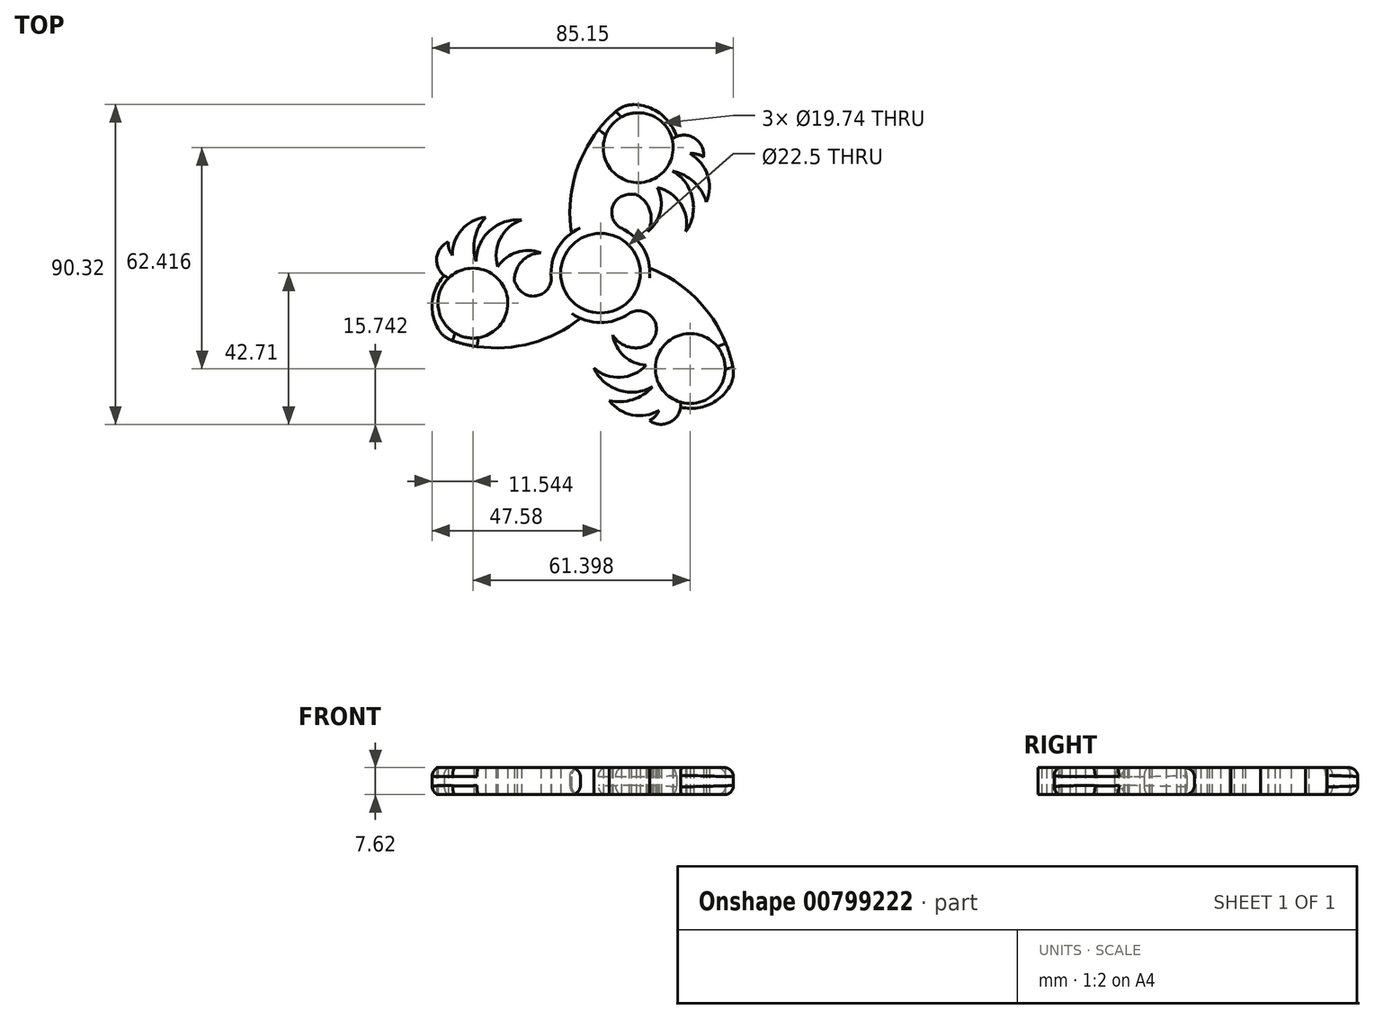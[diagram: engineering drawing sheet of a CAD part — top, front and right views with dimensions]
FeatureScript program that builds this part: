
annotation { "Feature Type Name" : "Feature", "Feature Type Description" : "" }
export const myFeature = defineFeature(function(context is Context, id is Id, definition is map)
    precondition{}
    {
        {
            var Q0;
            Q0=qCreatedBy(makeId("Top.planeOp"),FACE);
            var sketch = newSketch(context, id + "F0", { "sketchPlane" : qUnion([Q0])});
            skCircle(sketch, "E0", {"center": v(0, 0) * mm, "radius": 13.97 * mm});
            skCircle(sketch, "E1", {"center": v(0, 0) * mm, "radius": 11.25 * mm});
            skArc(sketch, "E2", {"start": v(6.16, 47.21) * mm, "mid": v(-5.92, 31.22) * mm, "end": v(-8.2, 11.3) * mm});
            skArc(sketch, "E3", {"start": v(8.66, 22.23) * mm, "mid": v(3.38, 18.59) * mm, "end": v(5.87, 12.68) * mm});
            skArc(sketch, "E4", {"start": v(8.66, 22.23) * mm, "mid": v(21.94, 36.17) * mm, "end": v(6.16, 47.21) * mm});
            skArc(sketch, "E5", {"start": v(13.38, 11.73) * mm, "mid": v(13.96, 17.7) * mm, "end": v(10.05, 22.23) * mm});
            skArc(sketch, "E6", {"start": v(13.38, 11.73) * mm, "mid": v(16.93, 17.48) * mm, "end": v(16.1, 24.18) * mm});
            skArc(sketch, "E7", {"start": v(24.13, 11.73) * mm, "mid": v(22.66, 19.6) * mm, "end": v(16.1, 24.18) * mm});
            skArc(sketch, "E8", {"start": v(24.13, 11.73) * mm, "mid": v(26.03, 21.08) * mm, "end": v(20.44, 28.8) * mm});
            skArc(sketch, "E9", {"start": v(29.93, 20.15) * mm, "mid": v(26.36, 25.77) * mm, "end": v(20.44, 28.8) * mm});
            skArc(sketch, "E10", {"start": v(29.93, 20.15) * mm, "mid": v(29.5, 29.45) * mm, "end": v(22, 34.96) * mm});
            skArc(sketch, "E11", {"start": v(29.15, 32.85) * mm, "mid": v(26.92, 37.87) * mm, "end": v(21.46, 38.58) * mm});
            skArc(sketch, "E12", {"start": v(29.15, 32.85) * mm, "mid": v(25.33, 33.77) * mm, "end": v(21.72, 32.23) * mm});
            skArc(sketch, "E13.1.0", {"start": v(-32.41, 15.84) * mm, "mid": v(-40.25, 10.82) * mm, "end": v(-41.28, 1.57) * mm});
            skArc(sketch, "E13.1.1", {"start": v(-22.22, 15.03) * mm, "mid": v(-31.27, 12) * mm, "end": v(-35.17, 3.3) * mm});
            skArc(sketch, "E13.1.2", {"start": v(-43.97, -18.27) * mm, "mid": v(-24.08, -20.73) * mm, "end": v(-5.69, -12.76) * mm});
            skArc(sketch, "E13.1.3", {"start": v(-32.41, 15.84) * mm, "mid": v(-35.5, 9.95) * mm, "end": v(-35.17, 3.3) * mm});
            skArc(sketch, "E13.1.4", {"start": v(-23.58, -3.61) * mm, "mid": v(-17.79, -6.37) * mm, "end": v(-13.91, -1.26) * mm});
            skArc(sketch, "E13.1.5", {"start": v(-43.03, 8.82) * mm, "mid": v(-46.26, 4.37) * mm, "end": v(-44.14, -0.7) * mm});
            skArc(sketch, "E13.1.6", {"start": v(-22.22, 15.03) * mm, "mid": v(-28.3, 9.82) * mm, "end": v(-28.99, 1.85) * mm});
            skArc(sketch, "E13.1.7", {"start": v(-23.58, -3.61) * mm, "mid": v(-42.3, 0.91) * mm, "end": v(-43.97, -18.27) * mm});
            skArc(sketch, "E13.1.8", {"start": v(-43.03, 8.82) * mm, "mid": v(-41.9, 5.06) * mm, "end": v(-38.77, 2.7) * mm});
            skArc(sketch, "E13.1.9", {"start": v(-16.85, 5.72) * mm, "mid": v(-23.6, 5.93) * mm, "end": v(-28.99, 1.85) * mm});
            skArc(sketch, "E13.1.10", {"start": v(-16.85, 5.72) * mm, "mid": v(-22.3, 3.24) * mm, "end": v(-24.28, -2.41) * mm});
            skArc(sketch, "E13.2.0", {"start": v(2.49, -36) * mm, "mid": v(10.75, -40.27) * mm, "end": v(19.28, -36.54) * mm});
            skArc(sketch, "E13.2.1", {"start": v(-1.9, -26.76) * mm, "mid": v(5.24, -33.08) * mm, "end": v(14.73, -32.1) * mm});
            skArc(sketch, "E13.2.2", {"start": v(37.8, -28.94) * mm, "mid": v(30, -10.48) * mm, "end": v(13.9, 1.45) * mm});
            skArc(sketch, "E13.2.3", {"start": v(2.49, -36) * mm, "mid": v(9.13, -35.71) * mm, "end": v(14.73, -32.1) * mm});
            skArc(sketch, "E13.2.4", {"start": v(14.92, -18.61) * mm, "mid": v(14.4, -12.22) * mm, "end": v(8.05, -11.42) * mm});
            skArc(sketch, "E13.2.5", {"start": v(13.87, -41.67) * mm, "mid": v(19.34, -42.25) * mm, "end": v(22.68, -37.87) * mm});
            skArc(sketch, "E13.2.6", {"start": v(-1.9, -26.76) * mm, "mid": v(5.64, -29.43) * mm, "end": v(12.9, -26.03) * mm});
            skArc(sketch, "E13.2.7", {"start": v(14.92, -18.61) * mm, "mid": v(20.36, -37.09) * mm, "end": v(37.8, -28.94) * mm});
            skArc(sketch, "E13.2.8", {"start": v(13.87, -41.67) * mm, "mid": v(16.58, -38.82) * mm, "end": v(17.06, -34.92) * mm});
            skArc(sketch, "E13.2.9", {"start": v(3.47, -17.46) * mm, "mid": v(6.67, -23.4) * mm, "end": v(12.9, -26.03) * mm});
            skArc(sketch, "E13.2.10", {"start": v(3.47, -17.46) * mm, "mid": v(8.34, -20.94) * mm, "end": v(14.23, -19.82) * mm});
            skCircle(sketch, "E14", {"center": v(10.67, 35.45) * mm, "radius": 9.87 * mm});
            skCircle(sketch, "E15.1.0", {"center": v(-36.04, -8.48) * mm, "radius": 9.87 * mm});
            skCircle(sketch, "E15.2.0", {"center": v(25.36, -26.97) * mm, "radius": 9.87 * mm});
            skSolve(sketch);
        }
        {
            var Q0;
            {var subQ3=sQuery(id+"F0.wireOp",EDGE,"E13.1.2");Q0=makeQuery(id+"F0.imprint","IMPRINT",FACE,{"disambiguationData":[TD([[makeQuery(id+"F0.imprint","IMPRINT",EDGE,{"derivedFrom":subQ3}),1.0]])]});}
            var Q1;
            Q1=makeQuery(id+"F0.imprint","IMPRINT",FACE,{"disambiguationData":[TD([[makeQuery(id+"F0.imprint","IMPRINT",EDGE,{"derivedFrom":sQuery(id+"F0.wireOp",EDGE,"E1")}),-1.0]])]});
            var Q2;
            {var subQ5=sQuery(id+"F0.wireOp",EDGE,"E13.1.5");Q2=makeQuery(id+"F0.imprint","IMPRINT",FACE,{"disambiguationData":[TD([[makeQuery(id+"F0.imprint","IMPRINT",EDGE,{"derivedFrom":subQ5}),1.0]])]});}
            var Q3;
            {var subQ0=sQuery(id+"F0.wireOp",EDGE,"E13.1.3");Q3=makeQuery(id+"F0.imprint","IMPRINT",FACE,{"disambiguationData":[TD([[makeQuery(id+"F0.imprint","IMPRINT",EDGE,{"derivedFrom":subQ0}),-1.0]])]});}
            var Q4;
            {var subQ0=sQuery(id+"F0.wireOp",EDGE,"E13.1.7");var subQ1=sQuery(id+"F0.wireOp",EDGE,"E13.1.0");var subQ2=makeQuery(id+"F0.imprint","INTERSECT",VERTEX,{"derivedFrom":[subQ1,subQ0]});Q4=makeQuery(id+"F0.imprint","IMPRINT",FACE,{"disambiguationData":[TD([[makeQuery(id+"F0.imprint","IMPRINT",EDGE,{"disambiguationData":[TD([[subQ2,1.0]])],"derivedFrom":subQ1}),1.0]])]});}
            var Q5;
            {var subQ0=sQuery(id+"F0.wireOp",EDGE,"E13.1.1");Q5=makeQuery(id+"F0.imprint","IMPRINT",FACE,{"disambiguationData":[TD([[makeQuery(id+"F0.imprint","IMPRINT",EDGE,{"derivedFrom":subQ0}),1.0]])]});}
            var Q6;
            {var subQ0=sQuery(id+"F0.wireOp",EDGE,"E13.1.9");Q6=makeQuery(id+"F0.imprint","IMPRINT",FACE,{"disambiguationData":[TD([[makeQuery(id+"F0.imprint","IMPRINT",EDGE,{"derivedFrom":subQ0}),1.0]])]});}
            var Q7;
            {var subQ3=sQuery(id+"F0.wireOp",EDGE,"E2");Q7=makeQuery(id+"F0.imprint","IMPRINT",FACE,{"disambiguationData":[TD([[makeQuery(id+"F0.imprint","IMPRINT",EDGE,{"derivedFrom":subQ3}),1.0]])]});}
            var Q8;
            {var subQ3=sQuery(id+"F0.wireOp",EDGE,"E13.2.2");Q8=makeQuery(id+"F0.imprint","IMPRINT",FACE,{"disambiguationData":[TD([[makeQuery(id+"F0.imprint","IMPRINT",EDGE,{"derivedFrom":subQ3}),1.0]])]});}
            var Q9;
            {var subQ3=sQuery(id+"F0.wireOp",EDGE,"E11");Q9=makeQuery(id+"F0.imprint","IMPRINT",FACE,{"disambiguationData":[TD([[makeQuery(id+"F0.imprint","IMPRINT",EDGE,{"derivedFrom":subQ3}),1.0]])]});}
            var Q10;
            {var subQ0=sQuery(id+"F0.wireOp",EDGE,"E9");Q10=makeQuery(id+"F0.imprint","IMPRINT",FACE,{"disambiguationData":[TD([[makeQuery(id+"F0.imprint","IMPRINT",EDGE,{"derivedFrom":subQ0}),-1.0]])]});}
            var Q11;
            {var subQ0=sQuery(id+"F0.wireOp",EDGE,"E7");Q11=makeQuery(id+"F0.imprint","IMPRINT",FACE,{"disambiguationData":[TD([[makeQuery(id+"F0.imprint","IMPRINT",EDGE,{"derivedFrom":subQ0}),-1.0]])]});}
            var Q12;
            {var subQ0=sQuery(id+"F0.wireOp",EDGE,"E5");Q12=makeQuery(id+"F0.imprint","IMPRINT",FACE,{"disambiguationData":[TD([[makeQuery(id+"F0.imprint","IMPRINT",EDGE,{"derivedFrom":subQ0}),-1.0]])]});}
            var Q13;
            {var subQ0=sQuery(id+"F0.wireOp",EDGE,"E10");var subQ1=sQuery(id+"F0.wireOp",EDGE,"E4");var subQ2=makeQuery(id+"F0.imprint","INTERSECT",VERTEX,{"derivedFrom":[subQ1,subQ0]});Q13=makeQuery(id+"F0.imprint","IMPRINT",FACE,{"disambiguationData":[TD([[makeQuery(id+"F0.imprint","IMPRINT",EDGE,{"disambiguationData":[TD([[subQ2,1.0]])],"derivedFrom":subQ1}),-1.0]])]});}
            var Q14;
            {var subQ0=sQuery(id+"F0.wireOp",EDGE,"E13.2.9");Q14=makeQuery(id+"F0.imprint","IMPRINT",FACE,{"disambiguationData":[TD([[makeQuery(id+"F0.imprint","IMPRINT",EDGE,{"derivedFrom":subQ0}),1.0]])]});}
            var Q15;
            {var subQ0=sQuery(id+"F0.wireOp",EDGE,"E13.2.1");Q15=makeQuery(id+"F0.imprint","IMPRINT",FACE,{"disambiguationData":[TD([[makeQuery(id+"F0.imprint","IMPRINT",EDGE,{"derivedFrom":subQ0}),1.0]])]});}
            var Q16;
            {var subQ5=sQuery(id+"F0.wireOp",EDGE,"E13.2.5");Q16=makeQuery(id+"F0.imprint","IMPRINT",FACE,{"disambiguationData":[TD([[makeQuery(id+"F0.imprint","IMPRINT",EDGE,{"derivedFrom":subQ5}),1.0]])]});}
            var Q17;
            {var subQ0=sQuery(id+"F0.wireOp",EDGE,"E13.2.3");Q17=makeQuery(id+"F0.imprint","IMPRINT",FACE,{"disambiguationData":[TD([[makeQuery(id+"F0.imprint","IMPRINT",EDGE,{"derivedFrom":subQ0}),-1.0]])]});}
            var Q18;
            {var subQ0=sQuery(id+"F0.wireOp",EDGE,"E13.2.7");var subQ1=sQuery(id+"F0.wireOp",EDGE,"E13.2.0");var subQ2=makeQuery(id+"F0.imprint","INTERSECT",VERTEX,{"derivedFrom":[subQ1,subQ0]});Q18=makeQuery(id+"F0.imprint","IMPRINT",FACE,{"disambiguationData":[TD([[makeQuery(id+"F0.imprint","IMPRINT",EDGE,{"disambiguationData":[TD([[subQ2,1.0]])],"derivedFrom":subQ1}),1.0]])]});}
            extrude(context, id + "F1", {"entities" : qUnion([Q0, Q1, Q2, Q3, Q4, Q5, Q6, Q7, Q8, Q9, Q10, Q11, Q12, Q13, Q14, Q15, Q16, Q17, Q18]), "depth" : 7.62 * mm, "offsetDistance" : 25.4 * mm});
        }
        {
            var Q0;
            Q0=makeQuery(id+"F1.opExtrude","SWEPT_EDGE",EDGE,{"disambiguationData":[OSD([sQuery(id+"F0.wireOp",EDGE,"E13.2.2"),sQuery(id+"F0.wireOp",EDGE,"E13.2.7")])]});
            var Q1;
            Q1=makeQuery(id+"F1.opExtrude","SWEPT_EDGE",EDGE,{"disambiguationData":[OSD([sQuery(id+"F0.wireOp",EDGE,"E2"),sQuery(id+"F0.wireOp",EDGE,"E4")])]});
            var Q2;
            Q2=makeQuery(id+"F1.opExtrude","SWEPT_EDGE",EDGE,{"disambiguationData":[OSD([sQuery(id+"F0.wireOp",EDGE,"E13.1.2"),sQuery(id+"F0.wireOp",EDGE,"E13.1.7")])]});
            fillet(context, id + "F2", {"entities" : qUnion([Q0, Q1, Q2]), "radius" : 7.62 * mm, "tangentPropagation" : true, "allowEdgeOverflow" : false});
        }
        {
            var Q0;
            {var subQ0=sQuery(id+"F0.wireOp",EDGE,"E13.1.7");var subQ1=sQuery(id+"F0.wireOp",EDGE,"E13.1.2");Q0=makeQuery(id+"F2.opFillet","BLEND_EDGE",EDGE,{"blendedFrom":[makeQuery(id+"F1.opExtrude","SWEPT_EDGE",EDGE,{"disambiguationData":[OSD([subQ1,subQ0])]}),makeQuery(id+"F1.opExtrude","CAP_FACE",FACE,{"disambiguationData":[OSD([sQuery(id+"F0.wireOp",EDGE,"E0"),sQuery(id+"F0.wireOp",EDGE,"E1"),sQuery(id+"F0.wireOp",EDGE,"E2"),sQuery(id+"F0.wireOp",EDGE,"E3"),sQuery(id+"F0.wireOp",EDGE,"E4"),sQuery(id+"F0.wireOp",EDGE,"E5"),sQuery(id+"F0.wireOp",EDGE,"E6"),sQuery(id+"F0.wireOp",EDGE,"E7"),sQuery(id+"F0.wireOp",EDGE,"E8"),sQuery(id+"F0.wireOp",EDGE,"E9"),sQuery(id+"F0.wireOp",EDGE,"E10"),sQuery(id+"F0.wireOp",EDGE,"E11"),sQuery(id+"F0.wireOp",EDGE,"E12"),sQuery(id+"F0.wireOp",EDGE,"E13.1.0"),sQuery(id+"F0.wireOp",EDGE,"E13.1.1"),subQ1,sQuery(id+"F0.wireOp",EDGE,"E13.1.3"),sQuery(id+"F0.wireOp",EDGE,"E13.1.4"),sQuery(id+"F0.wireOp",EDGE,"E13.1.5"),sQuery(id+"F0.wireOp",EDGE,"E13.1.6"),subQ0,sQuery(id+"F0.wireOp",EDGE,"E13.1.8"),sQuery(id+"F0.wireOp",EDGE,"E13.1.9"),sQuery(id+"F0.wireOp",EDGE,"E13.1.10"),sQuery(id+"F0.wireOp",EDGE,"E13.2.0"),sQuery(id+"F0.wireOp",EDGE,"E13.2.1"),sQuery(id+"F0.wireOp",EDGE,"E13.2.2"),sQuery(id+"F0.wireOp",EDGE,"E13.2.3"),sQuery(id+"F0.wireOp",EDGE,"E13.2.4"),sQuery(id+"F0.wireOp",EDGE,"E13.2.5"),sQuery(id+"F0.wireOp",EDGE,"E13.2.6"),sQuery(id+"F0.wireOp",EDGE,"E13.2.7"),sQuery(id+"F0.wireOp",EDGE,"E13.2.8"),sQuery(id+"F0.wireOp",EDGE,"E13.2.9"),sQuery(id+"F0.wireOp",EDGE,"E13.2.10"),sQuery(id+"F0.wireOp",EDGE,"E14"),sQuery(id+"F0.wireOp",EDGE,"E15.1.0"),sQuery(id+"F0.wireOp",EDGE,"E15.2.0")])],"isStart":false})],"blendedInto":[makeQuery(id+"F1.opExtrude","CAP_FACE",FACE,{"disambiguationData":[OSD([sQuery(id+"F0.wireOp",EDGE,"E0"),sQuery(id+"F0.wireOp",EDGE,"E1"),sQuery(id+"F0.wireOp",EDGE,"E2"),sQuery(id+"F0.wireOp",EDGE,"E3"),sQuery(id+"F0.wireOp",EDGE,"E4"),sQuery(id+"F0.wireOp",EDGE,"E5"),sQuery(id+"F0.wireOp",EDGE,"E6"),sQuery(id+"F0.wireOp",EDGE,"E7"),sQuery(id+"F0.wireOp",EDGE,"E8"),sQuery(id+"F0.wireOp",EDGE,"E9"),sQuery(id+"F0.wireOp",EDGE,"E10"),sQuery(id+"F0.wireOp",EDGE,"E11"),sQuery(id+"F0.wireOp",EDGE,"E12"),sQuery(id+"F0.wireOp",EDGE,"E13.1.0"),sQuery(id+"F0.wireOp",EDGE,"E13.1.1"),subQ1,sQuery(id+"F0.wireOp",EDGE,"E13.1.3"),sQuery(id+"F0.wireOp",EDGE,"E13.1.4"),sQuery(id+"F0.wireOp",EDGE,"E13.1.5"),sQuery(id+"F0.wireOp",EDGE,"E13.1.6"),subQ0,sQuery(id+"F0.wireOp",EDGE,"E13.1.8"),sQuery(id+"F0.wireOp",EDGE,"E13.1.9"),sQuery(id+"F0.wireOp",EDGE,"E13.1.10"),sQuery(id+"F0.wireOp",EDGE,"E13.2.0"),sQuery(id+"F0.wireOp",EDGE,"E13.2.1"),sQuery(id+"F0.wireOp",EDGE,"E13.2.2"),sQuery(id+"F0.wireOp",EDGE,"E13.2.3"),sQuery(id+"F0.wireOp",EDGE,"E13.2.4"),sQuery(id+"F0.wireOp",EDGE,"E13.2.5"),sQuery(id+"F0.wireOp",EDGE,"E13.2.6"),sQuery(id+"F0.wireOp",EDGE,"E13.2.7"),sQuery(id+"F0.wireOp",EDGE,"E13.2.8"),sQuery(id+"F0.wireOp",EDGE,"E13.2.9"),sQuery(id+"F0.wireOp",EDGE,"E13.2.10"),sQuery(id+"F0.wireOp",EDGE,"E14"),sQuery(id+"F0.wireOp",EDGE,"E15.1.0"),sQuery(id+"F0.wireOp",EDGE,"E15.2.0")])],"isStart":false})]});}
            var Q1;
            {var subQ0=sQuery(id+"F0.wireOp",EDGE,"E13.2.7");var subQ1=sQuery(id+"F0.wireOp",EDGE,"E13.2.2");Q1=makeQuery(id+"F2.opFillet","BLEND_EDGE",EDGE,{"blendedFrom":[makeQuery(id+"F1.opExtrude","SWEPT_EDGE",EDGE,{"disambiguationData":[OSD([subQ1,subQ0])]}),makeQuery(id+"F1.opExtrude","CAP_FACE",FACE,{"disambiguationData":[OSD([sQuery(id+"F0.wireOp",EDGE,"E0"),sQuery(id+"F0.wireOp",EDGE,"E1"),sQuery(id+"F0.wireOp",EDGE,"E2"),sQuery(id+"F0.wireOp",EDGE,"E3"),sQuery(id+"F0.wireOp",EDGE,"E4"),sQuery(id+"F0.wireOp",EDGE,"E5"),sQuery(id+"F0.wireOp",EDGE,"E6"),sQuery(id+"F0.wireOp",EDGE,"E7"),sQuery(id+"F0.wireOp",EDGE,"E8"),sQuery(id+"F0.wireOp",EDGE,"E9"),sQuery(id+"F0.wireOp",EDGE,"E10"),sQuery(id+"F0.wireOp",EDGE,"E11"),sQuery(id+"F0.wireOp",EDGE,"E12"),sQuery(id+"F0.wireOp",EDGE,"E13.1.0"),sQuery(id+"F0.wireOp",EDGE,"E13.1.1"),sQuery(id+"F0.wireOp",EDGE,"E13.1.2"),sQuery(id+"F0.wireOp",EDGE,"E13.1.3"),sQuery(id+"F0.wireOp",EDGE,"E13.1.4"),sQuery(id+"F0.wireOp",EDGE,"E13.1.5"),sQuery(id+"F0.wireOp",EDGE,"E13.1.6"),sQuery(id+"F0.wireOp",EDGE,"E13.1.7"),sQuery(id+"F0.wireOp",EDGE,"E13.1.8"),sQuery(id+"F0.wireOp",EDGE,"E13.1.9"),sQuery(id+"F0.wireOp",EDGE,"E13.1.10"),sQuery(id+"F0.wireOp",EDGE,"E13.2.0"),sQuery(id+"F0.wireOp",EDGE,"E13.2.1"),subQ1,sQuery(id+"F0.wireOp",EDGE,"E13.2.3"),sQuery(id+"F0.wireOp",EDGE,"E13.2.4"),sQuery(id+"F0.wireOp",EDGE,"E13.2.5"),sQuery(id+"F0.wireOp",EDGE,"E13.2.6"),subQ0,sQuery(id+"F0.wireOp",EDGE,"E13.2.8"),sQuery(id+"F0.wireOp",EDGE,"E13.2.9"),sQuery(id+"F0.wireOp",EDGE,"E13.2.10"),sQuery(id+"F0.wireOp",EDGE,"E14"),sQuery(id+"F0.wireOp",EDGE,"E15.1.0"),sQuery(id+"F0.wireOp",EDGE,"E15.2.0")])],"isStart":false})],"blendedInto":[makeQuery(id+"F1.opExtrude","CAP_FACE",FACE,{"disambiguationData":[OSD([sQuery(id+"F0.wireOp",EDGE,"E0"),sQuery(id+"F0.wireOp",EDGE,"E1"),sQuery(id+"F0.wireOp",EDGE,"E2"),sQuery(id+"F0.wireOp",EDGE,"E3"),sQuery(id+"F0.wireOp",EDGE,"E4"),sQuery(id+"F0.wireOp",EDGE,"E5"),sQuery(id+"F0.wireOp",EDGE,"E6"),sQuery(id+"F0.wireOp",EDGE,"E7"),sQuery(id+"F0.wireOp",EDGE,"E8"),sQuery(id+"F0.wireOp",EDGE,"E9"),sQuery(id+"F0.wireOp",EDGE,"E10"),sQuery(id+"F0.wireOp",EDGE,"E11"),sQuery(id+"F0.wireOp",EDGE,"E12"),sQuery(id+"F0.wireOp",EDGE,"E13.1.0"),sQuery(id+"F0.wireOp",EDGE,"E13.1.1"),sQuery(id+"F0.wireOp",EDGE,"E13.1.2"),sQuery(id+"F0.wireOp",EDGE,"E13.1.3"),sQuery(id+"F0.wireOp",EDGE,"E13.1.4"),sQuery(id+"F0.wireOp",EDGE,"E13.1.5"),sQuery(id+"F0.wireOp",EDGE,"E13.1.6"),sQuery(id+"F0.wireOp",EDGE,"E13.1.7"),sQuery(id+"F0.wireOp",EDGE,"E13.1.8"),sQuery(id+"F0.wireOp",EDGE,"E13.1.9"),sQuery(id+"F0.wireOp",EDGE,"E13.1.10"),sQuery(id+"F0.wireOp",EDGE,"E13.2.0"),sQuery(id+"F0.wireOp",EDGE,"E13.2.1"),subQ1,sQuery(id+"F0.wireOp",EDGE,"E13.2.3"),sQuery(id+"F0.wireOp",EDGE,"E13.2.4"),sQuery(id+"F0.wireOp",EDGE,"E13.2.5"),sQuery(id+"F0.wireOp",EDGE,"E13.2.6"),subQ0,sQuery(id+"F0.wireOp",EDGE,"E13.2.8"),sQuery(id+"F0.wireOp",EDGE,"E13.2.9"),sQuery(id+"F0.wireOp",EDGE,"E13.2.10"),sQuery(id+"F0.wireOp",EDGE,"E14"),sQuery(id+"F0.wireOp",EDGE,"E15.1.0"),sQuery(id+"F0.wireOp",EDGE,"E15.2.0")])],"isStart":false})]});}
            var Q2;
            {var subQ0=sQuery(id+"F0.wireOp",EDGE,"E4");var subQ1=sQuery(id+"F0.wireOp",EDGE,"E2");Q2=makeQuery(id+"F2.opFillet","BLEND_EDGE",EDGE,{"blendedFrom":[makeQuery(id+"F1.opExtrude","SWEPT_EDGE",EDGE,{"disambiguationData":[OSD([subQ1,subQ0])]}),makeQuery(id+"F1.opExtrude","CAP_FACE",FACE,{"disambiguationData":[OSD([sQuery(id+"F0.wireOp",EDGE,"E0"),sQuery(id+"F0.wireOp",EDGE,"E1"),subQ1,sQuery(id+"F0.wireOp",EDGE,"E3"),subQ0,sQuery(id+"F0.wireOp",EDGE,"E5"),sQuery(id+"F0.wireOp",EDGE,"E6"),sQuery(id+"F0.wireOp",EDGE,"E7"),sQuery(id+"F0.wireOp",EDGE,"E8"),sQuery(id+"F0.wireOp",EDGE,"E9"),sQuery(id+"F0.wireOp",EDGE,"E10"),sQuery(id+"F0.wireOp",EDGE,"E11"),sQuery(id+"F0.wireOp",EDGE,"E12"),sQuery(id+"F0.wireOp",EDGE,"E13.1.0"),sQuery(id+"F0.wireOp",EDGE,"E13.1.1"),sQuery(id+"F0.wireOp",EDGE,"E13.1.2"),sQuery(id+"F0.wireOp",EDGE,"E13.1.3"),sQuery(id+"F0.wireOp",EDGE,"E13.1.4"),sQuery(id+"F0.wireOp",EDGE,"E13.1.5"),sQuery(id+"F0.wireOp",EDGE,"E13.1.6"),sQuery(id+"F0.wireOp",EDGE,"E13.1.7"),sQuery(id+"F0.wireOp",EDGE,"E13.1.8"),sQuery(id+"F0.wireOp",EDGE,"E13.1.9"),sQuery(id+"F0.wireOp",EDGE,"E13.1.10"),sQuery(id+"F0.wireOp",EDGE,"E13.2.0"),sQuery(id+"F0.wireOp",EDGE,"E13.2.1"),sQuery(id+"F0.wireOp",EDGE,"E13.2.2"),sQuery(id+"F0.wireOp",EDGE,"E13.2.3"),sQuery(id+"F0.wireOp",EDGE,"E13.2.4"),sQuery(id+"F0.wireOp",EDGE,"E13.2.5"),sQuery(id+"F0.wireOp",EDGE,"E13.2.6"),sQuery(id+"F0.wireOp",EDGE,"E13.2.7"),sQuery(id+"F0.wireOp",EDGE,"E13.2.8"),sQuery(id+"F0.wireOp",EDGE,"E13.2.9"),sQuery(id+"F0.wireOp",EDGE,"E13.2.10"),sQuery(id+"F0.wireOp",EDGE,"E14"),sQuery(id+"F0.wireOp",EDGE,"E15.1.0"),sQuery(id+"F0.wireOp",EDGE,"E15.2.0")])],"isStart":false})],"blendedInto":[makeQuery(id+"F1.opExtrude","CAP_FACE",FACE,{"disambiguationData":[OSD([sQuery(id+"F0.wireOp",EDGE,"E0"),sQuery(id+"F0.wireOp",EDGE,"E1"),subQ1,sQuery(id+"F0.wireOp",EDGE,"E3"),subQ0,sQuery(id+"F0.wireOp",EDGE,"E5"),sQuery(id+"F0.wireOp",EDGE,"E6"),sQuery(id+"F0.wireOp",EDGE,"E7"),sQuery(id+"F0.wireOp",EDGE,"E8"),sQuery(id+"F0.wireOp",EDGE,"E9"),sQuery(id+"F0.wireOp",EDGE,"E10"),sQuery(id+"F0.wireOp",EDGE,"E11"),sQuery(id+"F0.wireOp",EDGE,"E12"),sQuery(id+"F0.wireOp",EDGE,"E13.1.0"),sQuery(id+"F0.wireOp",EDGE,"E13.1.1"),sQuery(id+"F0.wireOp",EDGE,"E13.1.2"),sQuery(id+"F0.wireOp",EDGE,"E13.1.3"),sQuery(id+"F0.wireOp",EDGE,"E13.1.4"),sQuery(id+"F0.wireOp",EDGE,"E13.1.5"),sQuery(id+"F0.wireOp",EDGE,"E13.1.6"),sQuery(id+"F0.wireOp",EDGE,"E13.1.7"),sQuery(id+"F0.wireOp",EDGE,"E13.1.8"),sQuery(id+"F0.wireOp",EDGE,"E13.1.9"),sQuery(id+"F0.wireOp",EDGE,"E13.1.10"),sQuery(id+"F0.wireOp",EDGE,"E13.2.0"),sQuery(id+"F0.wireOp",EDGE,"E13.2.1"),sQuery(id+"F0.wireOp",EDGE,"E13.2.2"),sQuery(id+"F0.wireOp",EDGE,"E13.2.3"),sQuery(id+"F0.wireOp",EDGE,"E13.2.4"),sQuery(id+"F0.wireOp",EDGE,"E13.2.5"),sQuery(id+"F0.wireOp",EDGE,"E13.2.6"),sQuery(id+"F0.wireOp",EDGE,"E13.2.7"),sQuery(id+"F0.wireOp",EDGE,"E13.2.8"),sQuery(id+"F0.wireOp",EDGE,"E13.2.9"),sQuery(id+"F0.wireOp",EDGE,"E13.2.10"),sQuery(id+"F0.wireOp",EDGE,"E14"),sQuery(id+"F0.wireOp",EDGE,"E15.1.0"),sQuery(id+"F0.wireOp",EDGE,"E15.2.0")])],"isStart":false})]});}
            fillet(context, id + "F3", {"entities" : qUnion([Q0, Q1, Q2]), "radius" : 2.54 * mm, "tangentPropagation" : true, "allowEdgeOverflow" : false});
        }
        {
            var Q0;
            {var subQ0=sQuery(id+"F0.wireOp",EDGE,"E4");var subQ1=sQuery(id+"F0.wireOp",EDGE,"E2");Q0=makeQuery(id+"F2.opFillet","BLEND_EDGE",EDGE,{"blendedFrom":[makeQuery(id+"F1.opExtrude","SWEPT_EDGE",EDGE,{"disambiguationData":[OSD([subQ1,subQ0])]}),makeQuery(id+"F1.opExtrude","CAP_FACE",FACE,{"disambiguationData":[OSD([sQuery(id+"F0.wireOp",EDGE,"E0"),sQuery(id+"F0.wireOp",EDGE,"E1"),subQ1,sQuery(id+"F0.wireOp",EDGE,"E3"),subQ0,sQuery(id+"F0.wireOp",EDGE,"E5"),sQuery(id+"F0.wireOp",EDGE,"E6"),sQuery(id+"F0.wireOp",EDGE,"E7"),sQuery(id+"F0.wireOp",EDGE,"E8"),sQuery(id+"F0.wireOp",EDGE,"E9"),sQuery(id+"F0.wireOp",EDGE,"E10"),sQuery(id+"F0.wireOp",EDGE,"E11"),sQuery(id+"F0.wireOp",EDGE,"E12"),sQuery(id+"F0.wireOp",EDGE,"E13.1.0"),sQuery(id+"F0.wireOp",EDGE,"E13.1.1"),sQuery(id+"F0.wireOp",EDGE,"E13.1.2"),sQuery(id+"F0.wireOp",EDGE,"E13.1.3"),sQuery(id+"F0.wireOp",EDGE,"E13.1.4"),sQuery(id+"F0.wireOp",EDGE,"E13.1.5"),sQuery(id+"F0.wireOp",EDGE,"E13.1.6"),sQuery(id+"F0.wireOp",EDGE,"E13.1.7"),sQuery(id+"F0.wireOp",EDGE,"E13.1.8"),sQuery(id+"F0.wireOp",EDGE,"E13.1.9"),sQuery(id+"F0.wireOp",EDGE,"E13.1.10"),sQuery(id+"F0.wireOp",EDGE,"E13.2.0"),sQuery(id+"F0.wireOp",EDGE,"E13.2.1"),sQuery(id+"F0.wireOp",EDGE,"E13.2.2"),sQuery(id+"F0.wireOp",EDGE,"E13.2.3"),sQuery(id+"F0.wireOp",EDGE,"E13.2.4"),sQuery(id+"F0.wireOp",EDGE,"E13.2.5"),sQuery(id+"F0.wireOp",EDGE,"E13.2.6"),sQuery(id+"F0.wireOp",EDGE,"E13.2.7"),sQuery(id+"F0.wireOp",EDGE,"E13.2.8"),sQuery(id+"F0.wireOp",EDGE,"E13.2.9"),sQuery(id+"F0.wireOp",EDGE,"E13.2.10"),sQuery(id+"F0.wireOp",EDGE,"E14"),sQuery(id+"F0.wireOp",EDGE,"E15.1.0"),sQuery(id+"F0.wireOp",EDGE,"E15.2.0")])],"isStart":true})],"blendedInto":[makeQuery(id+"F1.opExtrude","CAP_FACE",FACE,{"disambiguationData":[OSD([sQuery(id+"F0.wireOp",EDGE,"E0"),sQuery(id+"F0.wireOp",EDGE,"E1"),subQ1,sQuery(id+"F0.wireOp",EDGE,"E3"),subQ0,sQuery(id+"F0.wireOp",EDGE,"E5"),sQuery(id+"F0.wireOp",EDGE,"E6"),sQuery(id+"F0.wireOp",EDGE,"E7"),sQuery(id+"F0.wireOp",EDGE,"E8"),sQuery(id+"F0.wireOp",EDGE,"E9"),sQuery(id+"F0.wireOp",EDGE,"E10"),sQuery(id+"F0.wireOp",EDGE,"E11"),sQuery(id+"F0.wireOp",EDGE,"E12"),sQuery(id+"F0.wireOp",EDGE,"E13.1.0"),sQuery(id+"F0.wireOp",EDGE,"E13.1.1"),sQuery(id+"F0.wireOp",EDGE,"E13.1.2"),sQuery(id+"F0.wireOp",EDGE,"E13.1.3"),sQuery(id+"F0.wireOp",EDGE,"E13.1.4"),sQuery(id+"F0.wireOp",EDGE,"E13.1.5"),sQuery(id+"F0.wireOp",EDGE,"E13.1.6"),sQuery(id+"F0.wireOp",EDGE,"E13.1.7"),sQuery(id+"F0.wireOp",EDGE,"E13.1.8"),sQuery(id+"F0.wireOp",EDGE,"E13.1.9"),sQuery(id+"F0.wireOp",EDGE,"E13.1.10"),sQuery(id+"F0.wireOp",EDGE,"E13.2.0"),sQuery(id+"F0.wireOp",EDGE,"E13.2.1"),sQuery(id+"F0.wireOp",EDGE,"E13.2.2"),sQuery(id+"F0.wireOp",EDGE,"E13.2.3"),sQuery(id+"F0.wireOp",EDGE,"E13.2.4"),sQuery(id+"F0.wireOp",EDGE,"E13.2.5"),sQuery(id+"F0.wireOp",EDGE,"E13.2.6"),sQuery(id+"F0.wireOp",EDGE,"E13.2.7"),sQuery(id+"F0.wireOp",EDGE,"E13.2.8"),sQuery(id+"F0.wireOp",EDGE,"E13.2.9"),sQuery(id+"F0.wireOp",EDGE,"E13.2.10"),sQuery(id+"F0.wireOp",EDGE,"E14"),sQuery(id+"F0.wireOp",EDGE,"E15.1.0"),sQuery(id+"F0.wireOp",EDGE,"E15.2.0")])],"isStart":true})]});}
            var Q1;
            {var subQ0=sQuery(id+"F0.wireOp",EDGE,"E13.2.7");var subQ1=sQuery(id+"F0.wireOp",EDGE,"E13.2.2");Q1=makeQuery(id+"F2.opFillet","BLEND_EDGE",EDGE,{"blendedFrom":[makeQuery(id+"F1.opExtrude","SWEPT_EDGE",EDGE,{"disambiguationData":[OSD([subQ1,subQ0])]}),makeQuery(id+"F1.opExtrude","CAP_FACE",FACE,{"disambiguationData":[OSD([sQuery(id+"F0.wireOp",EDGE,"E0"),sQuery(id+"F0.wireOp",EDGE,"E1"),sQuery(id+"F0.wireOp",EDGE,"E2"),sQuery(id+"F0.wireOp",EDGE,"E3"),sQuery(id+"F0.wireOp",EDGE,"E4"),sQuery(id+"F0.wireOp",EDGE,"E5"),sQuery(id+"F0.wireOp",EDGE,"E6"),sQuery(id+"F0.wireOp",EDGE,"E7"),sQuery(id+"F0.wireOp",EDGE,"E8"),sQuery(id+"F0.wireOp",EDGE,"E9"),sQuery(id+"F0.wireOp",EDGE,"E10"),sQuery(id+"F0.wireOp",EDGE,"E11"),sQuery(id+"F0.wireOp",EDGE,"E12"),sQuery(id+"F0.wireOp",EDGE,"E13.1.0"),sQuery(id+"F0.wireOp",EDGE,"E13.1.1"),sQuery(id+"F0.wireOp",EDGE,"E13.1.2"),sQuery(id+"F0.wireOp",EDGE,"E13.1.3"),sQuery(id+"F0.wireOp",EDGE,"E13.1.4"),sQuery(id+"F0.wireOp",EDGE,"E13.1.5"),sQuery(id+"F0.wireOp",EDGE,"E13.1.6"),sQuery(id+"F0.wireOp",EDGE,"E13.1.7"),sQuery(id+"F0.wireOp",EDGE,"E13.1.8"),sQuery(id+"F0.wireOp",EDGE,"E13.1.9"),sQuery(id+"F0.wireOp",EDGE,"E13.1.10"),sQuery(id+"F0.wireOp",EDGE,"E13.2.0"),sQuery(id+"F0.wireOp",EDGE,"E13.2.1"),subQ1,sQuery(id+"F0.wireOp",EDGE,"E13.2.3"),sQuery(id+"F0.wireOp",EDGE,"E13.2.4"),sQuery(id+"F0.wireOp",EDGE,"E13.2.5"),sQuery(id+"F0.wireOp",EDGE,"E13.2.6"),subQ0,sQuery(id+"F0.wireOp",EDGE,"E13.2.8"),sQuery(id+"F0.wireOp",EDGE,"E13.2.9"),sQuery(id+"F0.wireOp",EDGE,"E13.2.10"),sQuery(id+"F0.wireOp",EDGE,"E14"),sQuery(id+"F0.wireOp",EDGE,"E15.1.0"),sQuery(id+"F0.wireOp",EDGE,"E15.2.0")])],"isStart":true})],"blendedInto":[makeQuery(id+"F1.opExtrude","CAP_FACE",FACE,{"disambiguationData":[OSD([sQuery(id+"F0.wireOp",EDGE,"E0"),sQuery(id+"F0.wireOp",EDGE,"E1"),sQuery(id+"F0.wireOp",EDGE,"E2"),sQuery(id+"F0.wireOp",EDGE,"E3"),sQuery(id+"F0.wireOp",EDGE,"E4"),sQuery(id+"F0.wireOp",EDGE,"E5"),sQuery(id+"F0.wireOp",EDGE,"E6"),sQuery(id+"F0.wireOp",EDGE,"E7"),sQuery(id+"F0.wireOp",EDGE,"E8"),sQuery(id+"F0.wireOp",EDGE,"E9"),sQuery(id+"F0.wireOp",EDGE,"E10"),sQuery(id+"F0.wireOp",EDGE,"E11"),sQuery(id+"F0.wireOp",EDGE,"E12"),sQuery(id+"F0.wireOp",EDGE,"E13.1.0"),sQuery(id+"F0.wireOp",EDGE,"E13.1.1"),sQuery(id+"F0.wireOp",EDGE,"E13.1.2"),sQuery(id+"F0.wireOp",EDGE,"E13.1.3"),sQuery(id+"F0.wireOp",EDGE,"E13.1.4"),sQuery(id+"F0.wireOp",EDGE,"E13.1.5"),sQuery(id+"F0.wireOp",EDGE,"E13.1.6"),sQuery(id+"F0.wireOp",EDGE,"E13.1.7"),sQuery(id+"F0.wireOp",EDGE,"E13.1.8"),sQuery(id+"F0.wireOp",EDGE,"E13.1.9"),sQuery(id+"F0.wireOp",EDGE,"E13.1.10"),sQuery(id+"F0.wireOp",EDGE,"E13.2.0"),sQuery(id+"F0.wireOp",EDGE,"E13.2.1"),subQ1,sQuery(id+"F0.wireOp",EDGE,"E13.2.3"),sQuery(id+"F0.wireOp",EDGE,"E13.2.4"),sQuery(id+"F0.wireOp",EDGE,"E13.2.5"),sQuery(id+"F0.wireOp",EDGE,"E13.2.6"),subQ0,sQuery(id+"F0.wireOp",EDGE,"E13.2.8"),sQuery(id+"F0.wireOp",EDGE,"E13.2.9"),sQuery(id+"F0.wireOp",EDGE,"E13.2.10"),sQuery(id+"F0.wireOp",EDGE,"E14"),sQuery(id+"F0.wireOp",EDGE,"E15.1.0"),sQuery(id+"F0.wireOp",EDGE,"E15.2.0")])],"isStart":true})]});}
            var Q2;
            {var subQ0=sQuery(id+"F0.wireOp",EDGE,"E13.1.7");var subQ1=sQuery(id+"F0.wireOp",EDGE,"E13.1.2");Q2=makeQuery(id+"F2.opFillet","BLEND_EDGE",EDGE,{"blendedFrom":[makeQuery(id+"F1.opExtrude","SWEPT_EDGE",EDGE,{"disambiguationData":[OSD([subQ1,subQ0])]}),makeQuery(id+"F1.opExtrude","CAP_FACE",FACE,{"disambiguationData":[OSD([sQuery(id+"F0.wireOp",EDGE,"E0"),sQuery(id+"F0.wireOp",EDGE,"E1"),sQuery(id+"F0.wireOp",EDGE,"E2"),sQuery(id+"F0.wireOp",EDGE,"E3"),sQuery(id+"F0.wireOp",EDGE,"E4"),sQuery(id+"F0.wireOp",EDGE,"E5"),sQuery(id+"F0.wireOp",EDGE,"E6"),sQuery(id+"F0.wireOp",EDGE,"E7"),sQuery(id+"F0.wireOp",EDGE,"E8"),sQuery(id+"F0.wireOp",EDGE,"E9"),sQuery(id+"F0.wireOp",EDGE,"E10"),sQuery(id+"F0.wireOp",EDGE,"E11"),sQuery(id+"F0.wireOp",EDGE,"E12"),sQuery(id+"F0.wireOp",EDGE,"E13.1.0"),sQuery(id+"F0.wireOp",EDGE,"E13.1.1"),subQ1,sQuery(id+"F0.wireOp",EDGE,"E13.1.3"),sQuery(id+"F0.wireOp",EDGE,"E13.1.4"),sQuery(id+"F0.wireOp",EDGE,"E13.1.5"),sQuery(id+"F0.wireOp",EDGE,"E13.1.6"),subQ0,sQuery(id+"F0.wireOp",EDGE,"E13.1.8"),sQuery(id+"F0.wireOp",EDGE,"E13.1.9"),sQuery(id+"F0.wireOp",EDGE,"E13.1.10"),sQuery(id+"F0.wireOp",EDGE,"E13.2.0"),sQuery(id+"F0.wireOp",EDGE,"E13.2.1"),sQuery(id+"F0.wireOp",EDGE,"E13.2.2"),sQuery(id+"F0.wireOp",EDGE,"E13.2.3"),sQuery(id+"F0.wireOp",EDGE,"E13.2.4"),sQuery(id+"F0.wireOp",EDGE,"E13.2.5"),sQuery(id+"F0.wireOp",EDGE,"E13.2.6"),sQuery(id+"F0.wireOp",EDGE,"E13.2.7"),sQuery(id+"F0.wireOp",EDGE,"E13.2.8"),sQuery(id+"F0.wireOp",EDGE,"E13.2.9"),sQuery(id+"F0.wireOp",EDGE,"E13.2.10"),sQuery(id+"F0.wireOp",EDGE,"E14"),sQuery(id+"F0.wireOp",EDGE,"E15.1.0"),sQuery(id+"F0.wireOp",EDGE,"E15.2.0")])],"isStart":true})],"blendedInto":[makeQuery(id+"F1.opExtrude","CAP_FACE",FACE,{"disambiguationData":[OSD([sQuery(id+"F0.wireOp",EDGE,"E0"),sQuery(id+"F0.wireOp",EDGE,"E1"),sQuery(id+"F0.wireOp",EDGE,"E2"),sQuery(id+"F0.wireOp",EDGE,"E3"),sQuery(id+"F0.wireOp",EDGE,"E4"),sQuery(id+"F0.wireOp",EDGE,"E5"),sQuery(id+"F0.wireOp",EDGE,"E6"),sQuery(id+"F0.wireOp",EDGE,"E7"),sQuery(id+"F0.wireOp",EDGE,"E8"),sQuery(id+"F0.wireOp",EDGE,"E9"),sQuery(id+"F0.wireOp",EDGE,"E10"),sQuery(id+"F0.wireOp",EDGE,"E11"),sQuery(id+"F0.wireOp",EDGE,"E12"),sQuery(id+"F0.wireOp",EDGE,"E13.1.0"),sQuery(id+"F0.wireOp",EDGE,"E13.1.1"),subQ1,sQuery(id+"F0.wireOp",EDGE,"E13.1.3"),sQuery(id+"F0.wireOp",EDGE,"E13.1.4"),sQuery(id+"F0.wireOp",EDGE,"E13.1.5"),sQuery(id+"F0.wireOp",EDGE,"E13.1.6"),subQ0,sQuery(id+"F0.wireOp",EDGE,"E13.1.8"),sQuery(id+"F0.wireOp",EDGE,"E13.1.9"),sQuery(id+"F0.wireOp",EDGE,"E13.1.10"),sQuery(id+"F0.wireOp",EDGE,"E13.2.0"),sQuery(id+"F0.wireOp",EDGE,"E13.2.1"),sQuery(id+"F0.wireOp",EDGE,"E13.2.2"),sQuery(id+"F0.wireOp",EDGE,"E13.2.3"),sQuery(id+"F0.wireOp",EDGE,"E13.2.4"),sQuery(id+"F0.wireOp",EDGE,"E13.2.5"),sQuery(id+"F0.wireOp",EDGE,"E13.2.6"),sQuery(id+"F0.wireOp",EDGE,"E13.2.7"),sQuery(id+"F0.wireOp",EDGE,"E13.2.8"),sQuery(id+"F0.wireOp",EDGE,"E13.2.9"),sQuery(id+"F0.wireOp",EDGE,"E13.2.10"),sQuery(id+"F0.wireOp",EDGE,"E14"),sQuery(id+"F0.wireOp",EDGE,"E15.1.0"),sQuery(id+"F0.wireOp",EDGE,"E15.2.0")])],"isStart":true})]});}
            fillet(context, id + "F4", {"entities" : qUnion([Q0, Q1, Q2]), "radius" : 2.54 * mm, "tangentPropagation" : true, "allowEdgeOverflow" : false});
        }
    });
